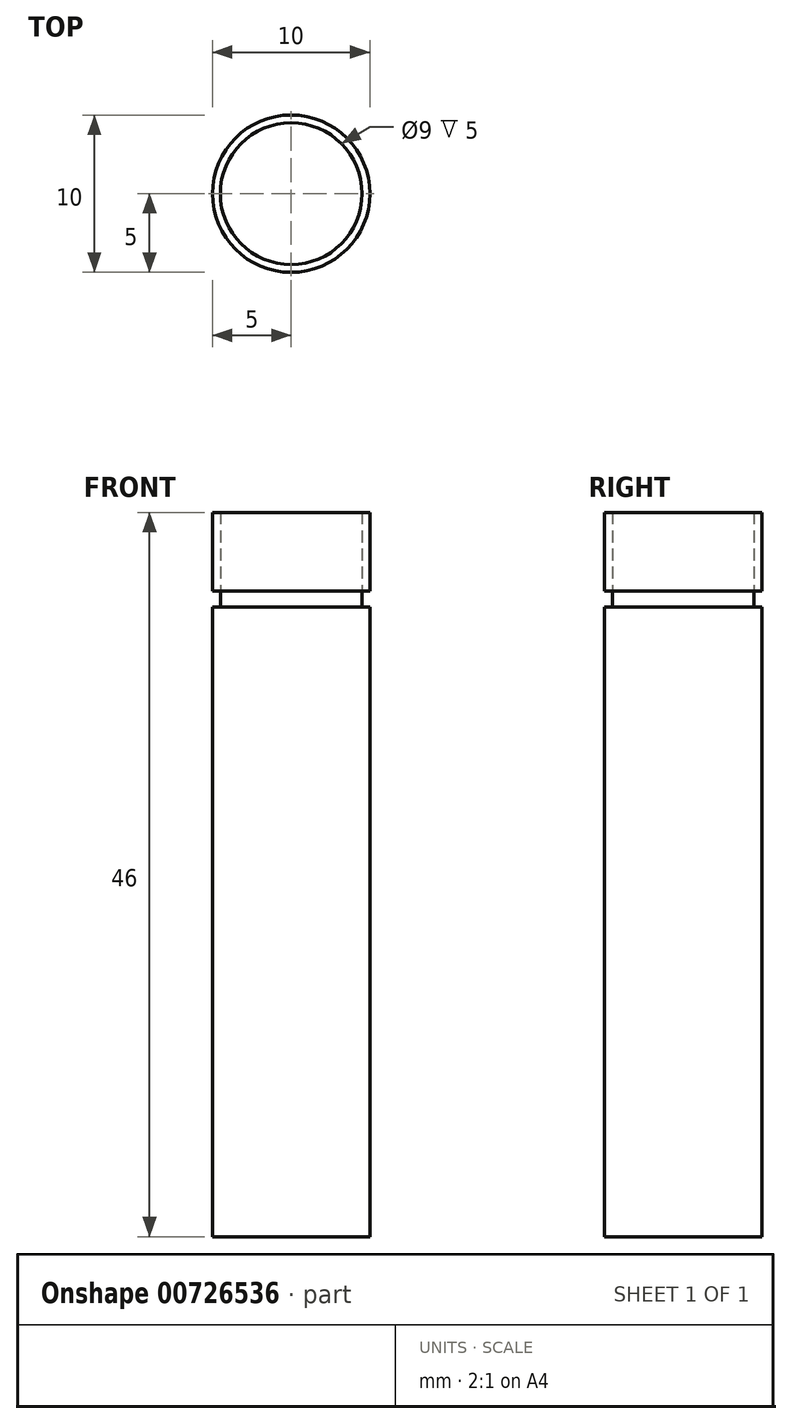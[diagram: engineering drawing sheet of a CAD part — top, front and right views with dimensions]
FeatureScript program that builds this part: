
annotation { "Feature Type Name" : "Feature", "Feature Type Description" : "" }
export const myFeature = defineFeature(function(context is Context, id is Id, definition is map)
    precondition{}
    {
        {
            var Q0;
            Q0=qCreatedBy(makeId("Top.planeOp"),FACE);
            var sketch = newSketch(context, id + "F0", { "sketchPlane" : qUnion([Q0])});
            skCircle(sketch, "E0", {"center": v(0, 0) * mm, "radius": 5 * mm});
            skSolve(sketch);
        }
        {
            var Q0;
            Q0=makeQuery(id+"F0.imprint","IMPRINT",FACE,{"disambiguationData":[TD([[makeQuery(id+"F0.imprint","IMPRINT",EDGE,{"derivedFrom":sQuery(id+"F0.wireOp",EDGE,"E0")}),1.0]])]});
            extrude(context, id + "F1", {"entities" : qUnion([Q0]), "depth" : 40 * mm, "offsetDistance" : 25 * mm});
        }
        {
            var Q0;
            Q0=makeQuery(id+"F1.opExtrude","CAP_FACE",FACE,{"disambiguationData":[OSD([sQuery(id+"F0.wireOp",EDGE,"E0")])],"isStart":false});
            var sketch = newSketch(context, id + "F2", { "sketchPlane" : qUnion([Q0])});
            skCircle(sketch, "E1", {"center": v(0, 0) * mm, "radius": 4.5 * mm});
            skSolve(sketch);
        }
        {
            var Q0;
            Q0=makeQuery(id+"F2.imprint","IMPRINT",FACE,{"disambiguationData":[TD([[makeQuery(id+"F2.imprint","IMPRINT",EDGE,{"derivedFrom":sQuery(id+"F2.wireOp",EDGE,"E1")}),1.0]])]});
            extrude(context, id + "F3", {"entities" : qUnion([Q0]), "operationType" : NewBodyOperationType.ADD, "depth" : 1 * mm, "offsetDistance" : 25 * mm});
        }
        {
            var Q0;
            Q0=makeQuery(id+"F3.opExtrude","CAP_FACE",FACE,{"disambiguationData":[OSD([sQuery(id+"F2.wireOp",EDGE,"E1")])],"isStart":false});
            var sketch = newSketch(context, id + "F4", { "sketchPlane" : qUnion([Q0])});
            skCircle(sketch, "E2", {"center": v(0, 0) * mm, "radius": 5 * mm});
            skSolve(sketch);
        }
        {
            var Q0;
            Q0=makeQuery(id+"F4.imprint","IMPRINT",FACE,{"disambiguationData":[TD([[makeQuery(id+"F4.imprint","IMPRINT",EDGE,{"derivedFrom":sQuery(id+"F4.wireOp",EDGE,"E2")}),1.0]])]});
            extrude(context, id + "F5", {"entities" : qUnion([Q0]), "depth" : 5 * mm, "offsetDistance" : 25 * mm});
        }
    });
